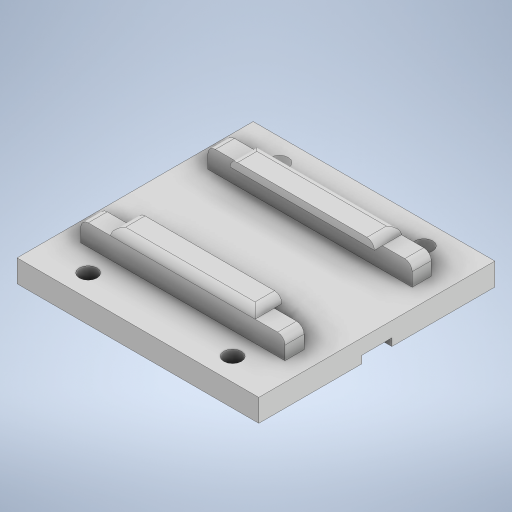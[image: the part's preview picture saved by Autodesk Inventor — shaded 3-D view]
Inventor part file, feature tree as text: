
AUTODESK INVENTOR PART (.ipt)
format: ipt  version: 2024 (Build 280153000, 153)  size: 435,712 bytes
history: native  units: in
note: dims shown in document units (in); Inventor stores cm internally (conversion verified against a paired STEP export)
features: projected_geometry x8, extrude x6, sketch x6, fillet x3
ambient origin geometry x8: Origin, YZ Plane, XZ Plane, XY Plane, X Axis, Y Axis, Z Axis, Center Point
bodies: Solid1 (feature_tree)
feature tree (23):
  extrude  "Extrusion1"  Depth=0.673in
  extrude  "Extrusion2"  Depth=0.2in
  extrude  "Extrusion4"  Depth=0.1in TaperAngle=0.0deg
  fillet  "Fillet1"  Radius=0.05in
  fillet  "Fillet3"  Radius=0.14in
  extrude  "Extrusion7"  Depth=0.1in
  fillet  "Fillet4"  Radius=0.05in
  extrude  "Extrusion8"  Depth=0.4in
  extrude  "Extrusion9"  Depth=0.1in
  sketch  "Sketch12"  dims[d35=0.4in d36=0.1in d37=0.1in d38=0.0275in d39=0.0275in d40=0.05in d41=0.2in d42=0.2in d43=0.18in d44=0.05in d45=0.0in d46=0.05in d47=0.125in d48=0.125in d49=0.125in d50=0.125in d51=0.15in d52=0.0in d53=0.15in d54=0.0in]
  sketch  "Sketch1"  dims[d0=1.26in d1=0.673in]
  sketch  "Sketch4"  dims[d2=0.4in d3=0.2in]
  projected_geometry  "Projected Loop1"
  projected_geometry  "Projected Loop9"
  sketch  "Sketch8"  dims[d4=0.1181in d5=0.1in d6=0.0in d10=0.05in d12=0.14in d13=0.0in]
  sketch  "Sketch9"  dims[d16=0.1in d17=0.1in d18=0.05in d19=0.0in]
  projected_geometry  "Projected Loop10"
  projected_geometry  "Projected Loop11"
  projected_geometry  "Projected Loop12"
  sketch  "Sketch11"  dims[d22=0.25in d34=0.4in]
  projected_geometry  "Projected Loop13"
  projected_geometry  "Projected Loop14"
  projected_geometry  "Projected Loop15"
